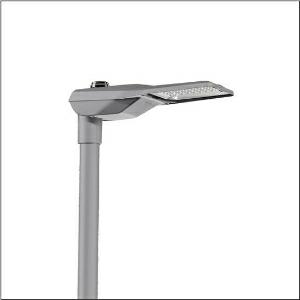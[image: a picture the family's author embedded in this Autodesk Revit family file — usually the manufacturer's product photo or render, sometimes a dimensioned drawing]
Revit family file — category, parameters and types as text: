
# Revit family: streetlight_sl_21_mini___st0_8a_5xe6c37n08jb_d8d6
name_source: partatom
category: Lighting Fixtures
units: mm (PartAtom-declared; Revit-internal decimal feet)

## family parameters
Cut with Voids When Loaded = No
Host = Face
Light Source = No
Part Type = Normal
Room Calculation Point = No
Round Connector Dimension = Use Diameter
Shared = No

## types (1)
- --- (1 x LED, 12830 lm, 87.3 W, 3000K)
    Apparent Load = 87 VA
    CIE Flux Codes = 41 75 97 100 100
    Color Rendering = 70
    Color Temperature = 3000K
    Default Elevation = 1800 mm
    Description = Streetlight SL 21 mini, mast luminaire, primary light control with lens, of PMMA, primary optical cover: cover, of toughened safety glass, transparent, light distribution: ST0.8a, light emission: direct distribution, primary light characteristic: asymmetric, installation type: side-entry, LED, 3G 2.5mm², High Power LED, rated luminous flux: 12.830lm, luminous efficacy: 147lm/W, light colour: 730, colour temperature: 3000K, control gear: NEMA (7pin), control: overheat protection, pre-setting: linear dimming characteristic, constant luminous flux control, time-dependent luminous flux control, flexible luminous flux parameterisation, mains connection: 230..240V, AC, 50/60Hz, connection cable pre-assembled, cable length: 10,5m, wiring characteristics: H05VV-F, start of lifetime: 87W, end of service life: 90W, reduction: 40W, luminaire housing, of diecast aluminium (EN AC-44300), powder-coated, Siteco® metallic grey (DB 702S), corrosivity category C5 mid according to DIN EN ISO 12944, multi-level sealing system, sealing non-destructively replaceable, inclination adjustable: 0°, 5°, 10°, 15°, length: 628mm, width: 235mm, height: 110mm, spigot size: 42mm (side-entry), mounting height: 4..8m, protection rating (complete): IP66, insulation class (complete): insulation class I (protective earthing), certification: CE, ENEC, ENEC+, VDE, impact resistance: IK10, permissible operating ambient temperature for outdoor applications: -40..+50°C, standard-compliant lighting for roads and squares, packaging unit: 1 piece

Light Distribution: ST0.8a
    Height = 110 mm
    Lamp = 1 x LED
    Lamp Light Flux = 12830 lm
    Lamp Power = 87.3 W
    Lamp count = 1
    Length = 625 mm
    Luminous efficacy = 147 lm/W
    Manufacturer = Siteco
    ModVariant = No
    Model = 5XE6C37N08JB
    Number of Poles = 1
    OnlyDefault = Yes
    Power Factor = 1
    Product Name = Streetlight SL 21 mini | ST0.8a
    Product group = mast luminaire | pylon top
    ProductGroupID = 6100
    Protection Class = Protection class I
    Protection Degree = IP 66
    RLX_Detail_Level = 1
    RLX_Emergency_Light_Flux = 0 lm
    RLX_Emergency_Type = 0
    RLX_Emergency_Type_DB = No
    RlxData = <blob elided: 26045 chars, md5=8efd084c>
    Socket = socket
    Standby Power = 0 W
    System Light Flux = 12830 lm
    System Power = 87 W
    Type Comments = factory setting: luminous flux: 100 % | dim-lin: 254 | 915 mA
    Type Image = l_1294379.jpg
    URL = http://relux.com
    VarID = @adj_155431
    Voltage = 0 V
    Weight = 0.00 kg
    Width = 234 mm

## geometry (parser evidence)
native form markers: Blend x4, Sweep x10
no freeform markers — native parametric forms only
